# Revit family: Electrical-Distribution_ABB_RELIAMOD-1000-1200A-RELT-MAIN-BRKR
name_source: partatom
category: Electrical Equipment
units: mm (PartAtom-declared; Revit-internal decimal feet)

## family parameters
Cut with Voids When Loaded = No
Host = Face
OmniClass Number = 23.35.29.11
OmniClass Title = Air Circuit Breakers
Panel Configuration = Two Columns, Circuits Across
Part Type = Panelboard
Room Calculation Point = No
Round Connector Dimension = Use Diameter
Shared = No

## types (8) — shared parameters
Apparent Load = 0 VA
Date Updated = 2023/08/07
Default Elevation = 4' - 0"
Enclosure = N3R Outdoor
Feed location = Bottom/Top
Main module type = Breaker
Manufacturer = ABB
Primary material = ABB - Steel - White
Product data url = https://www.bimobject.com
URL = https://new.abb.com
Version = 1
zero-valued in all types: Power Factor

## per-type parameters (varying)
| type | Arc reduction | Description | Frames | ICRating | Main amperage | Main circuit breaker trip unit | Number of Poles | Phase | Voltage | Voltage (V) |
| RMM1BL10R | - | RELIAMOD 1PH 1000A 65K RELT MAIN BRKR | XT7S | 65 | 1000 A | Ekip Dip LS/I | 2 | 1-Phase 3-Wire | 120/240V | 120 V |
| RMM1BH10R | - | RELIAMOD 1PH 1000A 100K RELT MAIN BRKR | XT7H | 100 | 1000 A | Ekip Dip LS/I | 2 | 1-Phase 3-Wire | 120/240V | 120 V |
| RMM1BL12R | Includes Arc Reduction (RELT) to meet NEC 240.87 | RELIAMOD 1PH 1200A 65K RELT MAIN BRKR | XT7S | 65 | 1200 A | Ekip Touch LSI | 2 | 1-Phase 3-Wire | 120/240V | 120 V |
| RMM1BH12R | Includes Arc Reduction (RELT) to meet NEC 240.87 | RELIAMOD 1PH 1200A 100K RELT MAIN BRKR | XT7H | 100 | 1200 A | Ekip Touch LSI | 2 | 1-Phase 3-Wire | 120/240V | 120 V |
| RMM3BL10R | - | RELIAMOD 3PH 1000A 65K RELT MAIN BRKR | XT7S | 65 | 1000 A | Ekip Dip LS/I | 3 | 3-Phase 4-Wire | 208Y/120V | 208 V |
| RMM3BH10R | - | RELIAMOD 3PH 1000A 100K RELT MAIN BRKR | XT7H | 100 | 1000 A | Ekip Dip LS/I | 3 | 3-Phase 4-Wire | 208Y/120V | 208 V |
| RMM3BL12R | Includes Arc Reduction (RELT) to meet NEC 240.87 | RELIAMOD 3PH 1200A 65K RELT MAIN BRKR | XT7S | 65 | 1200 A | Ekip Touch LSI | 3 | 3-Phase 4-Wire | 208Y/120V | 208 V |
| RMM3BH12R | Includes Arc Reduction (RELT) to meet NEC 240.87 | RELIAMOD 3PH 1200A 100K RELT MAIN BRKR | XT7H | 100 | 1200 A | Ekip Touch LSI | 3 | 3-Phase 4-Wire | 208Y/120V | 208 V |

note: column(s) folded — value = type name in every type: Model

## geometry (parser evidence)
native form markers: Sweep x18
no freeform markers — native parametric forms only
